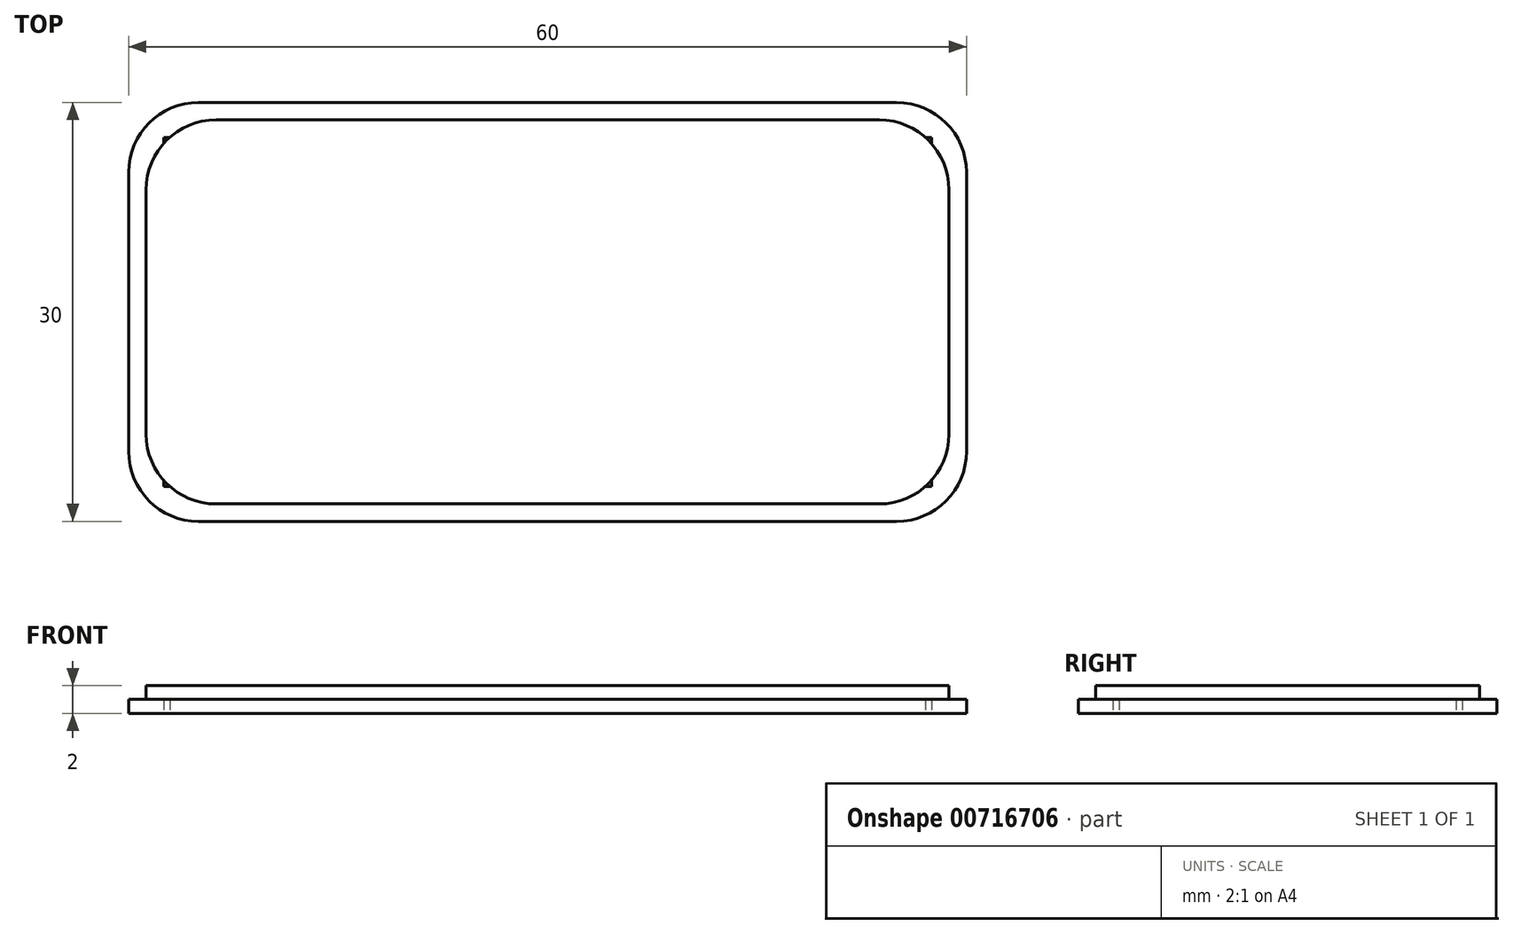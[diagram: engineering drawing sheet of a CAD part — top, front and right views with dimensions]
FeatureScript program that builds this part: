
annotation { "Feature Type Name" : "Feature", "Feature Type Description" : "" }
export const myFeature = defineFeature(function(context is Context, id is Id, definition is map)
    precondition{}
    {
        {
            var Q0;
            Q0=qCreatedBy(makeId("Top.planeOp"),FACE);
            var sketch = newSketch(context, id + "F0", { "sketchPlane" : qUnion([Q0])});
            skLineSegment(sketch, "E0.bottom", {"start": v(-25, 15) * mm, "end": v(25, 15) * mm});
            skLineSegment(sketch, "E0.top", {"start": v(-25, -15) * mm, "end": v(25, -15) * mm});
            skLineSegment(sketch, "E0.left", {"start": v(-30, 10) * mm, "end": v(-30, -10) * mm});
            skLineSegment(sketch, "E0.right", {"start": v(30, 10) * mm, "end": v(30, -10) * mm});
            skPoint(sketch, "E0.middle", {"position": v(0, 0) * mm});
            skLineSegment(sketch, "E1.bottom", {"start": v(-27.5, 12.5) * mm, "end": v(27.5, 12.5) * mm});
            skLineSegment(sketch, "E1.top", {"start": v(-27.5, -12.5) * mm, "end": v(27.5, -12.5) * mm});
            skLineSegment(sketch, "E1.left", {"start": v(-27.5, 12.5) * mm, "end": v(-27.5, -12.5) * mm});
            skLineSegment(sketch, "E1.right", {"start": v(27.5, 12.5) * mm, "end": v(27.5, -12.5) * mm});
            skLineSegment(sketch, "E2.bottom", {"start": v(23.75, 13.75) * mm, "end": v(-23.75, 13.75) * mm});
            skLineSegment(sketch, "E2.top", {"start": v(23.75, -13.75) * mm, "end": v(-23.75, -13.75) * mm});
            skLineSegment(sketch, "E2.left", {"start": v(28.75, 8.75) * mm, "end": v(28.75, -8.75) * mm});
            skLineSegment(sketch, "E2.right", {"start": v(-28.75, 8.75) * mm, "end": v(-28.75, -8.75) * mm});
            skPoint(sketch, "E3.visualSharp", {"position": v(30, 15) * mm});
            skArc(sketch, "E3.filletArc", {"start": v(30, 10) * mm, "mid": v(28.54, 13.54) * mm, "end": v(25, 15) * mm});
            skPoint(sketch, "E4.visualSharp", {"position": v(30, -15) * mm});
            skArc(sketch, "E4.filletArc", {"start": v(25, -15) * mm, "mid": v(28.54, -13.54) * mm, "end": v(30, -10) * mm});
            skPoint(sketch, "E5.visualSharp", {"position": v(-30, 15) * mm});
            skArc(sketch, "E5.filletArc", {"start": v(-25, 15) * mm, "mid": v(-28.54, 13.54) * mm, "end": v(-30, 10) * mm});
            skPoint(sketch, "E6.visualSharp", {"position": v(-30, -15) * mm});
            skArc(sketch, "E6.filletArc", {"start": v(-30, -10) * mm, "mid": v(-28.54, -13.54) * mm, "end": v(-25, -15) * mm});
            skPoint(sketch, "E7.visualSharp", {"position": v(28.75, 13.75) * mm});
            skArc(sketch, "E7.filletArc", {"start": v(28.75, 8.75) * mm, "mid": v(27.29, 12.29) * mm, "end": v(23.75, 13.75) * mm});
            skPoint(sketch, "E8.visualSharp", {"position": v(28.75, -13.75) * mm});
            skArc(sketch, "E8.filletArc", {"start": v(23.75, -13.75) * mm, "mid": v(27.29, -12.29) * mm, "end": v(28.75, -8.75) * mm});
            skPoint(sketch, "E9.visualSharp", {"position": v(-28.75, 13.75) * mm});
            skArc(sketch, "E9.filletArc", {"start": v(-23.75, 13.75) * mm, "mid": v(-27.29, 12.29) * mm, "end": v(-28.75, 8.75) * mm});
            skPoint(sketch, "E10.visualSharp", {"position": v(-28.75, -13.75) * mm});
            skArc(sketch, "E10.filletArc", {"start": v(-28.75, -8.75) * mm, "mid": v(-27.29, -12.29) * mm, "end": v(-23.75, -13.75) * mm});
            skSolve(sketch);
        }
        {
            var Q0;
            Q0=makeQuery(id+"F0.imprint","IMPRINT",FACE,{"disambiguationData":[TD([[makeQuery(id+"F0.imprint","IMPRINT",EDGE,{"derivedFrom":sQuery(id+"F0.wireOp",EDGE,"E0.bottom")}),-1.0]])]});
            extrude(context, id + "F1", {"entities" : qUnion([Q0]), "depth" : 1 * mm, "offsetDistance" : 25 * mm});
        }
        {
            var Q0;
            {var subQ5=sQuery(id+"F0.wireOp",EDGE,"E1.bottom");var subQ7=sQuery(id+"F0.wireOp",EDGE,"E9.filletArc");var subQ15=makeQuery(id+"F0.imprint","INTERSECT",VERTEX,{"derivedFrom":[subQ5,subQ7]});Q0=makeQuery(id+"F0.imprint","IMPRINT",FACE,{"disambiguationData":[TD([[makeQuery(id+"F0.imprint","IMPRINT",EDGE,{"disambiguationData":[TD([[subQ15,-1.0]])],"derivedFrom":subQ5}),-1.0]])]});}
            var Q1;
            {var subQ5=sQuery(id+"F0.wireOp",EDGE,"E2.left");Q1=makeQuery(id+"F0.imprint","IMPRINT",FACE,{"disambiguationData":[TD([[makeQuery(id+"F0.imprint","IMPRINT",EDGE,{"derivedFrom":subQ5}),-1.0]])]});}
            var Q2;
            {var subQ5=sQuery(id+"F0.wireOp",EDGE,"E2.bottom");Q2=makeQuery(id+"F0.imprint","IMPRINT",FACE,{"disambiguationData":[TD([[makeQuery(id+"F0.imprint","IMPRINT",EDGE,{"derivedFrom":subQ5}),1.0]])]});}
            var Q3;
            {var subQ5=sQuery(id+"F0.wireOp",EDGE,"E2.top");Q3=makeQuery(id+"F0.imprint","IMPRINT",FACE,{"disambiguationData":[TD([[makeQuery(id+"F0.imprint","IMPRINT",EDGE,{"derivedFrom":subQ5}),-1.0]])]});}
            var Q4;
            {var subQ5=sQuery(id+"F0.wireOp",EDGE,"E2.right");Q4=makeQuery(id+"F0.imprint","IMPRINT",FACE,{"disambiguationData":[TD([[makeQuery(id+"F0.imprint","IMPRINT",EDGE,{"derivedFrom":subQ5}),1.0]])]});}
            extrude(context, id + "F2", {"entities" : qUnion([Q0, Q1, Q2, Q3, Q4]), "operationType" : NewBodyOperationType.ADD, "depth" : 2 * mm, "offsetDistance" : 25 * mm});
        }
    });
